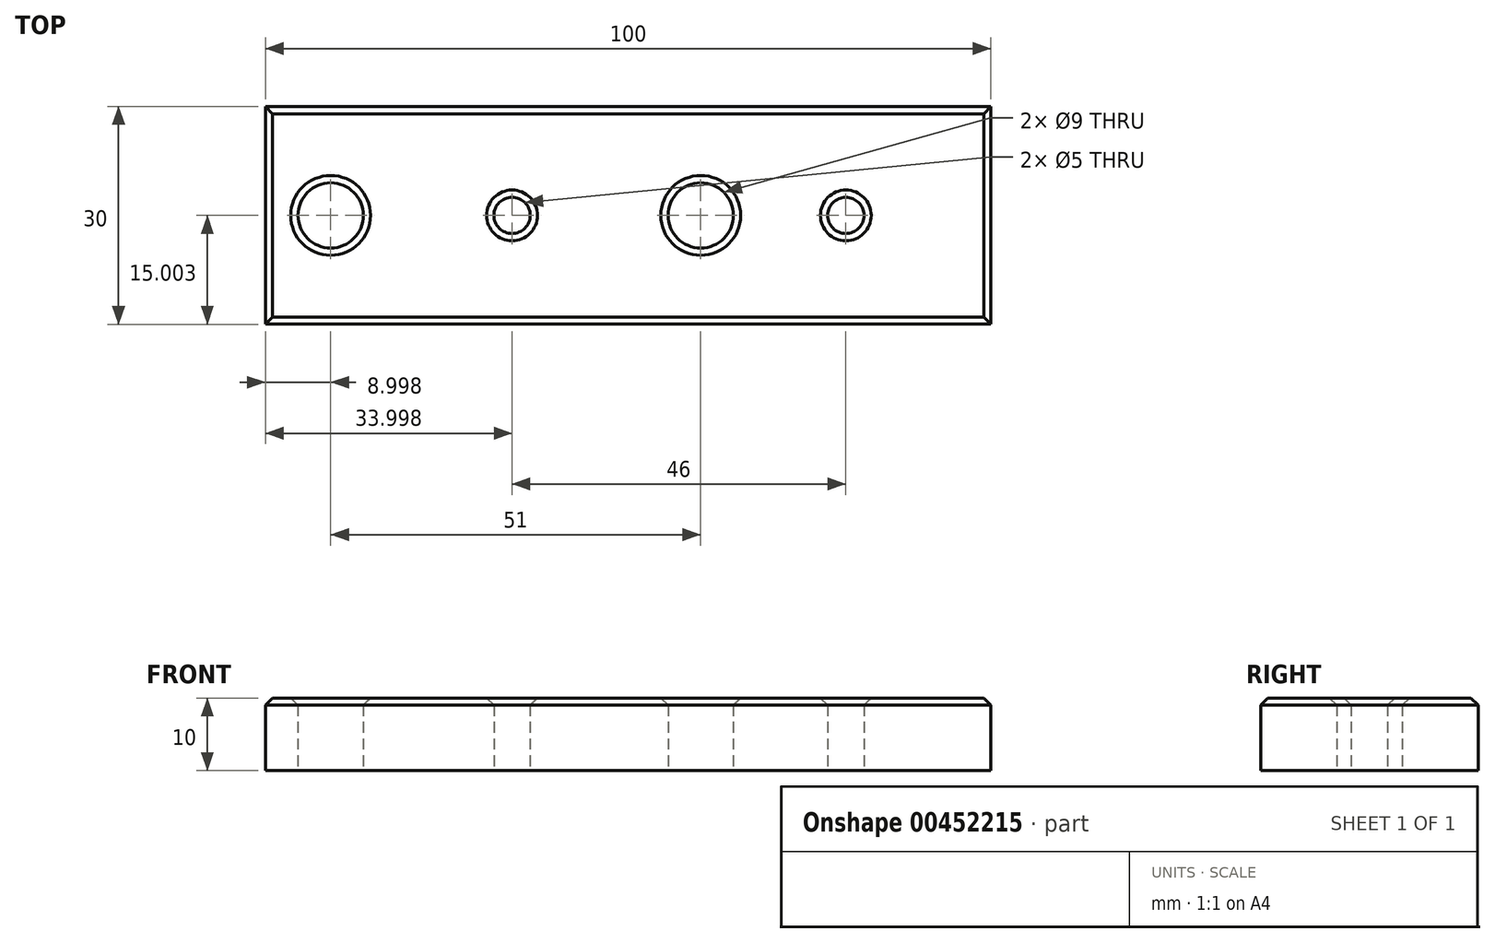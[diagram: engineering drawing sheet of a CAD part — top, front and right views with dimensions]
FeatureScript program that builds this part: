
annotation { "Feature Type Name" : "Feature", "Feature Type Description" : "" }
export const myFeature = defineFeature(function(context is Context, id is Id, definition is map)
    precondition{}
    {
        {
            var Q0;
            Q0=qCreatedBy(makeId("Top.planeOp"),FACE);
            var sketch = newSketch(context, id + "F0", { "sketchPlane" : qUnion([Q0])});
            skLineSegment(sketch, "E0.bottom", {"start": v(-50.4, -10) * mm, "end": v(49.6, -10) * mm});
            skLineSegment(sketch, "E0.top", {"start": v(-50.4, 20) * mm, "end": v(49.6, 20) * mm});
            skLineSegment(sketch, "E0.left", {"start": v(-50.4, -10) * mm, "end": v(-50.4, 20) * mm});
            skLineSegment(sketch, "E0.right", {"start": v(49.6, -10) * mm, "end": v(49.6, 20) * mm});
            skLineSegment(sketch, "E1", {"start": v(-50.4, 5) * mm, "end": v(49.6, 5) * mm, "construction": true});
            skCircle(sketch, "E2", {"center": v(-41.4, 5) * mm, "radius": 4.5 * mm});
            skCircle(sketch, "E3", {"center": v(-16.4, 5) * mm, "radius": 2.5 * mm});
            skCircle(sketch, "E4", {"center": v(9.6, 5) * mm, "radius": 4.5 * mm});
            skCircle(sketch, "E5", {"center": v(29.6, 5) * mm, "radius": 2.5 * mm});
            skSolve(sketch);
        }
        {
            var Q0;
            Q0=makeQuery(id+"F0.imprint","IMPRINT",FACE,{"disambiguationData":[TD([[makeQuery(id+"F0.imprint","IMPRINT",EDGE,{"derivedFrom":sQuery(id+"F0.wireOp",EDGE,"E0.bottom")}),1.0]])]});
            extrude(context, id + "F1", {"entities" : qUnion([Q0]), "depth" : 10 * mm});
        }
        {
            var Q0;
            Q0=makeQuery(id+"F1.opExtrude","CAP_EDGE",EDGE,{"disambiguationData":[OSD([sQuery(id+"F0.wireOp",EDGE,"E0.bottom")])],"isStart":false});
            var Q1;
            Q1=makeQuery(id+"F1.opExtrude","CAP_EDGE",EDGE,{"disambiguationData":[OSD([sQuery(id+"F0.wireOp",EDGE,"E0.left")])],"isStart":false});
            var Q2;
            Q2=makeQuery(id+"F1.opExtrude","CAP_EDGE",EDGE,{"disambiguationData":[OSD([sQuery(id+"F0.wireOp",EDGE,"E0.top")])],"isStart":false});
            var Q3;
            Q3=makeQuery(id+"F1.opExtrude","CAP_EDGE",EDGE,{"disambiguationData":[OSD([sQuery(id+"F0.wireOp",EDGE,"E0.right")])],"isStart":false});
            chamfer(context, id + "F2", {"entities" : qUnion([Q0, Q1, Q2, Q3]), "width" : 1 * mm, "tangentPropagation" : true});
        }
        {
            var Q0;
            Q0=makeQuery(id+"F1.opExtrude","CAP_EDGE",EDGE,{"disambiguationData":[OSD([sQuery(id+"F0.wireOp",EDGE,"E2")])],"isStart":false});
            var Q1;
            Q1=makeQuery(id+"F1.opExtrude","CAP_EDGE",EDGE,{"disambiguationData":[OSD([sQuery(id+"F0.wireOp",EDGE,"E3")])],"isStart":false});
            var Q2;
            Q2=makeQuery(id+"F1.opExtrude","CAP_EDGE",EDGE,{"disambiguationData":[OSD([sQuery(id+"F0.wireOp",EDGE,"E4")])],"isStart":false});
            var Q3;
            Q3=makeQuery(id+"F1.opExtrude","CAP_EDGE",EDGE,{"disambiguationData":[OSD([sQuery(id+"F0.wireOp",EDGE,"E5")])],"isStart":false});
            chamfer(context, id + "F3", {"entities" : qUnion([Q0, Q1, Q2, Q3]), "width" : 1 * mm, "tangentPropagation" : true});
        }
    });
